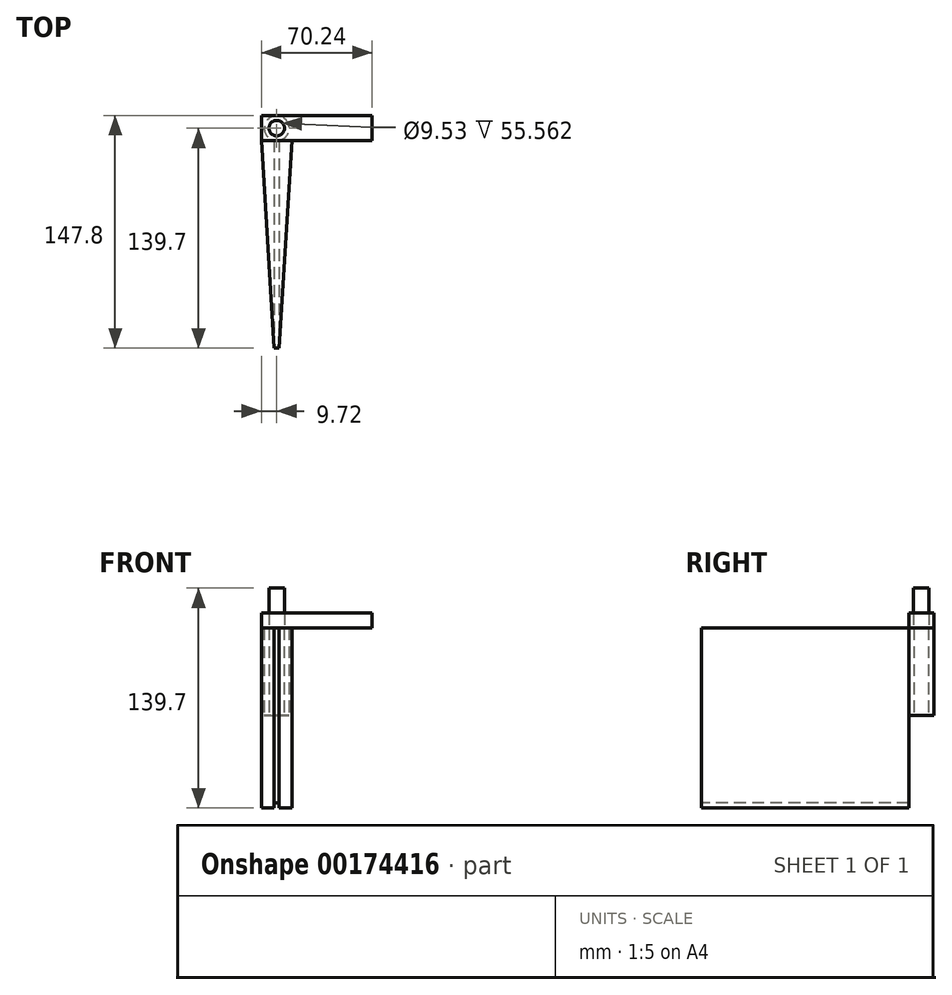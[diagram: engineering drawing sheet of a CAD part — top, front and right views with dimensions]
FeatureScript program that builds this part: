
annotation { "Feature Type Name" : "Feature", "Feature Type Description" : "" }
export const myFeature = defineFeature(function(context is Context, id is Id, definition is map)
    precondition{}
    {
        {
            var Q0;
            Q0=qCreatedBy(makeId("Top.planeOp"),FACE);
            var sketch = newSketch(context, id + "F0", { "sketchPlane" : qUnion([Q0])});
            skCircle(sketch, "E0", {"center": v(0, 0) * mm, "radius": 7.94 * mm});
            skCircle(sketch, "E1", {"center": v(0, 0) * mm, "radius": 4.76 * mm});
            skLineSegment(sketch, "E2.top", {"start": v(1.59, -139.7) * mm, "end": v(-1.59, -139.7) * mm});
            skLineSegment(sketch, "E2.left", {"start": v(1.59, 0) * mm, "end": v(1.59, -139.7) * mm});
            skLineSegment(sketch, "E2.right", {"start": v(-1.59, 0) * mm, "end": v(-1.59, -139.7) * mm});
            skLineSegment(sketch, "E3", {"start": v(-4.76, 0) * mm, "end": v(4.76, 0) * mm});
            skPoint(sketch, "E2.bottom.end.orphan", {"position": v(-1.59, 139.7) * mm});
            skPoint(sketch, "E2.bottom.start.orphan", {"position": v(1.59, 139.7) * mm});
            skSolve(sketch);
        }
        {
            var Q0;
            Q0 = qSketchRegion(id + "F0", true);
            extrude(context, id + "F1", {"entities" : qUnion([Q0]), "depth" : 55.56 * mm});
        }
        {
            var Q0;
            Q0=makeQuery(id+"F1.opExtrude","CAP_FACE",FACE,{"disambiguationData":[OSD([sQuery(id+"F0.wireOp",EDGE,"E0"),sQuery(id+"F0.wireOp",EDGE,"E1"),sQuery(id+"F0.wireOp",EDGE,"E2.top"),sQuery(id+"F0.wireOp",EDGE,"E2.left"),sQuery(id+"F0.wireOp",EDGE,"E2.right")])],"isStart":true});
            var sketch = newSketch(context, id + "F2", { "sketchPlane" : qUnion([Q0])});
            skLineSegment(sketch, "E4.bottom", {"start": v(-1.59, 7.78) * mm, "end": v(1.59, 7.78) * mm});
            skLineSegment(sketch, "E4.top", {"start": v(-1.59, 139.7) * mm, "end": v(1.59, 139.7) * mm});
            skLineSegment(sketch, "E4.left", {"start": v(-1.59, 7.78) * mm, "end": v(-1.59, 139.7) * mm});
            skLineSegment(sketch, "E4.right", {"start": v(1.59, 7.78) * mm, "end": v(1.59, 139.7) * mm});
            skSolve(sketch);
        }
        {
            var Q0;
            Q0 = qSketchRegion(id + "F2", true);
            extrude(context, id + "F3", {"entities" : qUnion([Q0]), "operationType" : NewBodyOperationType.ADD, "depth" : 55.56 * mm});
        }
        {
            var Q0;
            Q0=makeQuery(id+"F1.opExtrude","CAP_FACE",FACE,{"disambiguationData":[OSD([sQuery(id+"F0.wireOp",EDGE,"E0"),sQuery(id+"F0.wireOp",EDGE,"E1"),sQuery(id+"F0.wireOp",EDGE,"E2.top"),sQuery(id+"F0.wireOp",EDGE,"E2.left"),sQuery(id+"F0.wireOp",EDGE,"E2.right")])],"isStart":false});
            var sketch = newSketch(context, id + "F4", { "sketchPlane" : qUnion([Q0])});
            skLineSegment(sketch, "E5", {"start": v(-1.59, -7.78) * mm, "end": v(-9.72, -7.78) * mm});
            skLineSegment(sketch, "E6", {"start": v(1.59, -7.78) * mm, "end": v(9.72, -7.78) * mm});
            skLineSegment(sketch, "E7", {"start": v(-9.72, -7.78) * mm, "end": v(-1.59, -139.7) * mm});
            skLineSegment(sketch, "E8", {"start": v(-1.59, -139.7) * mm, "end": v(-1.59, -7.78) * mm});
            skLineSegment(sketch, "E9", {"start": v(9.72, -7.78) * mm, "end": v(1.59, -139.7) * mm});
            skLineSegment(sketch, "E10", {"start": v(1.59, -139.7) * mm, "end": v(1.59, -7.78) * mm});
            skSolve(sketch);
        }
        {
            var Q0;
            Q0 = qSketchRegion(id + "F4", true);
            extrude(context, id + "F5", {"entities" : qUnion([Q0]), "operationType" : NewBodyOperationType.ADD, "oppositeDirection" : true, "depth" : 114.3 * mm});
        }
        {
            var Q0;
            Q0=makeQuery(id+"F5.boolean.opBoolean","MERGE",FACE,{"derivedFrom":[makeQuery(id+"F1.opExtrude","CAP_FACE",FACE,{"disambiguationData":[OSD([sQuery(id+"F0.wireOp",EDGE,"E0"),sQuery(id+"F0.wireOp",EDGE,"E1"),sQuery(id+"F0.wireOp",EDGE,"E2.top"),sQuery(id+"F0.wireOp",EDGE,"E2.left"),sQuery(id+"F0.wireOp",EDGE,"E2.right")])],"isStart":false}),makeQuery(id+"F5.opExtrude","CAP_FACE",FACE,{"disambiguationData":[OSD([sQuery(id+"F4.wireOp",EDGE,"E5"),sQuery(id+"F4.wireOp",EDGE,"E7"),sQuery(id+"F4.wireOp",EDGE,"E8")])],"isStart":true}),makeQuery(id+"F5.opExtrude","CAP_FACE",FACE,{"disambiguationData":[OSD([sQuery(id+"F4.wireOp",EDGE,"E6"),sQuery(id+"F4.wireOp",EDGE,"E9"),sQuery(id+"F4.wireOp",EDGE,"E10")])],"isStart":true})]});
            var sketch = newSketch(context, id + "F6", { "sketchPlane" : qUnion([Q0])});
            skCircle(sketch, "E11", {"center": v(0, 0) * mm, "radius": 4.93 * mm});
            skSolve(sketch);
        }
        {
            var Q0;
            Q0 = qSketchRegion(id + "F6", true);
            extrude(context, id + "F7", {"entities" : qUnion([Q0]), "operationType" : NewBodyOperationType.ADD, "depth" : 25.4 * mm});
        }
        {
            var Q0;
            Q0=makeQuery(id+"F5.boolean.opBoolean","MERGE",FACE,{"derivedFrom":[makeQuery(id+"F1.opExtrude","CAP_FACE",FACE,{"disambiguationData":[OSD([sQuery(id+"F0.wireOp",EDGE,"E0"),sQuery(id+"F0.wireOp",EDGE,"E1"),sQuery(id+"F0.wireOp",EDGE,"E2.top"),sQuery(id+"F0.wireOp",EDGE,"E2.left"),sQuery(id+"F0.wireOp",EDGE,"E2.right")])],"isStart":false}),makeQuery(id+"F5.opExtrude","CAP_FACE",FACE,{"disambiguationData":[OSD([sQuery(id+"F4.wireOp",EDGE,"E5"),sQuery(id+"F4.wireOp",EDGE,"E7"),sQuery(id+"F4.wireOp",EDGE,"E8")])],"isStart":true}),makeQuery(id+"F5.opExtrude","CAP_FACE",FACE,{"disambiguationData":[OSD([sQuery(id+"F4.wireOp",EDGE,"E6"),sQuery(id+"F4.wireOp",EDGE,"E9"),sQuery(id+"F4.wireOp",EDGE,"E10")])],"isStart":true})]});
            var sketch = newSketch(context, id + "F8", { "sketchPlane" : qUnion([Q0])});
            skLineSegment(sketch, "E12.bottom", {"start": v(-9.72, -7.78) * mm, "end": v(9.72, -7.78) * mm});
            skLineSegment(sketch, "E12.top", {"start": v(-9.72, 8.1) * mm, "end": v(9.72, 8.1) * mm});
            skLineSegment(sketch, "E12.left", {"start": v(-9.72, -7.78) * mm, "end": v(-9.72, 8.1) * mm});
            skLineSegment(sketch, "E13.bottom", {"start": v(9.72, 8.1) * mm, "end": v(60.52, 8.1) * mm});
            skLineSegment(sketch, "E13.top", {"start": v(9.72, -7.78) * mm, "end": v(60.52, -7.78) * mm});
            skLineSegment(sketch, "E13.right", {"start": v(60.52, 8.1) * mm, "end": v(60.52, -7.78) * mm});
            skSolve(sketch);
        }
        {
            var Q0;
            Q0 = qSketchRegion(id + "F8", true);
            extrude(context, id + "F9", {"entities" : qUnion([Q0]), "depth" : 9.52 * mm});
        }
    });
